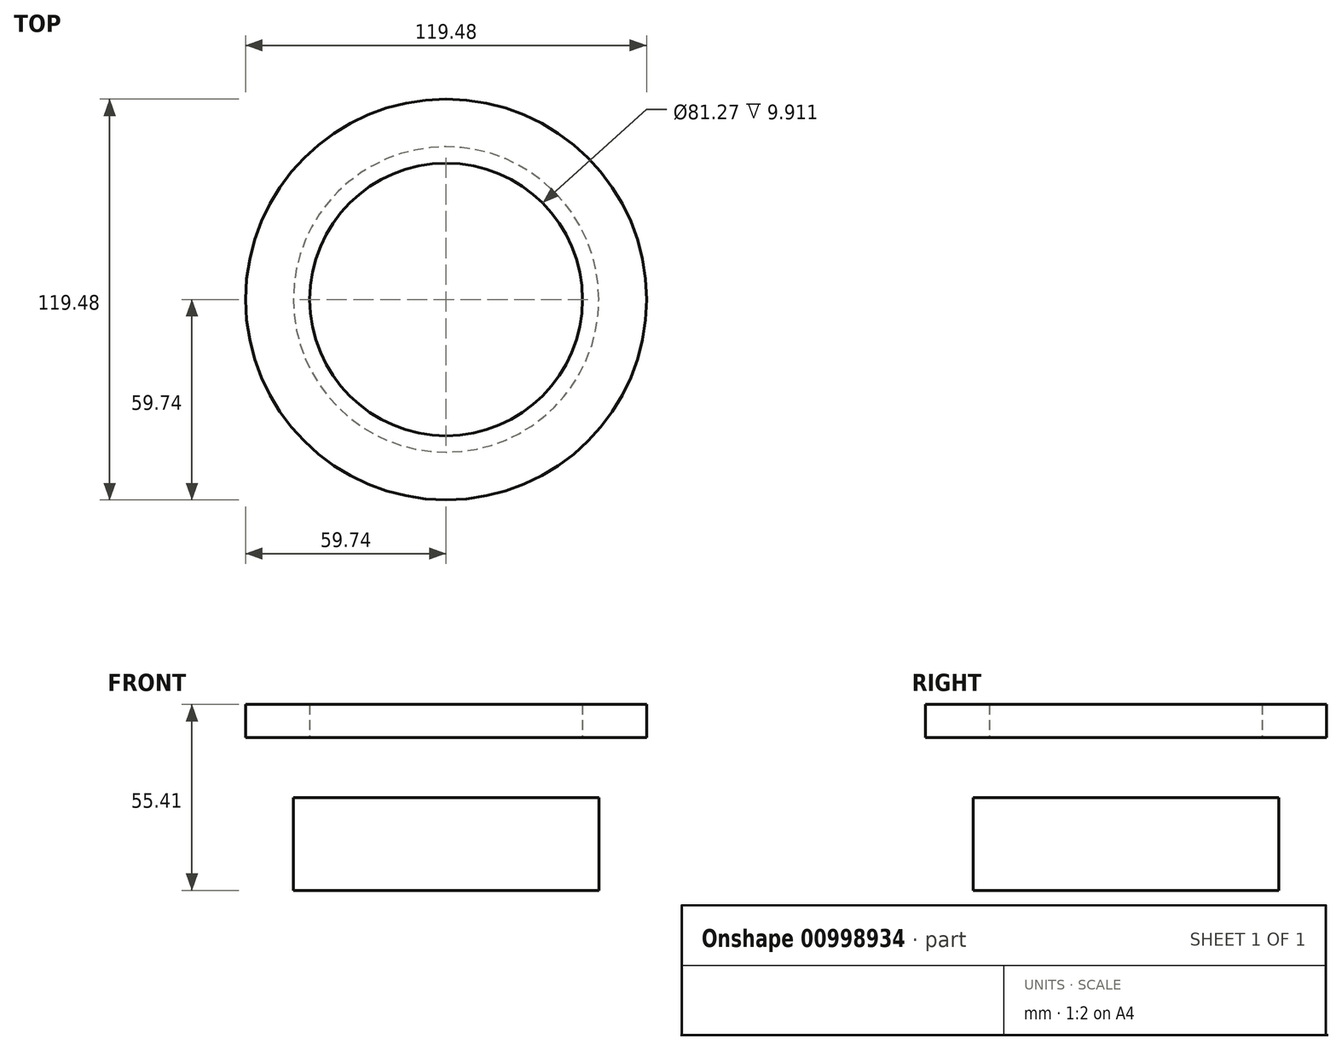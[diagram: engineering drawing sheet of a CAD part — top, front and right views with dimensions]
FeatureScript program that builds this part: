
annotation { "Feature Type Name" : "Feature", "Feature Type Description" : "" }
export const myFeature = defineFeature(function(context is Context, id is Id, definition is map)
    precondition{}
    {
        {
            var Q0;
            Q0=qCreatedBy(makeId("Front.planeOp"),FACE);
            var sketch = newSketch(context, id + "F0", { "sketchPlane" : qUnion([Q0])});
            skLineSegment(sketch, "E0.bottom", {"start": v(0, 0) * mm, "end": v(45.5, 0) * mm});
            skLineSegment(sketch, "E0.top", {"start": v(0, 27.66) * mm, "end": v(45.5, 27.66) * mm});
            skLineSegment(sketch, "E0.left", {"start": v(0, 0) * mm, "end": v(0, 27.66) * mm});
            skLineSegment(sketch, "E0.right", {"start": v(45.5, 0) * mm, "end": v(45.5, 27.66) * mm});
            skLineSegment(sketch, "E1.bottom", {"start": v(59.74, 55.41) * mm, "end": v(40.64, 55.41) * mm});
            skLineSegment(sketch, "E1.top", {"start": v(59.74, 45.5) * mm, "end": v(40.64, 45.5) * mm});
            skLineSegment(sketch, "E1.left", {"start": v(59.74, 55.41) * mm, "end": v(59.74, 45.5) * mm});
            skLineSegment(sketch, "E1.right", {"start": v(40.64, 55.41) * mm, "end": v(40.64, 45.5) * mm});
            skLineSegment(sketch, "E2", {"start": v(0, 0) * mm, "end": v(0, 79.92) * mm, "construction": true});
            skSolve(sketch);
        }
        {
            var Q0;
            Q0=makeQuery(id+"F0.imprint","IMPRINT",FACE,{"disambiguationData":[TD([[makeQuery(id+"F0.imprint","IMPRINT",EDGE,{"derivedFrom":sQuery(id+"F0.wireOp",EDGE,"E0.bottom")}),1.0]])]});
            var Q1;
            Q1=makeQuery(id+"F0.imprint","IMPRINT",FACE,{"disambiguationData":[TD([[makeQuery(id+"F0.imprint","IMPRINT",EDGE,{"derivedFrom":sQuery(id+"F0.wireOp",EDGE,"E1.bottom")}),1.0]])]});
            var Q2;
            Q2=sQuery(id+"F0.wireOp",EDGE,"E2");
            revolve(context, id + "F1", {"surfaceOperationType" : NewSurfaceOperationType.NEW, "entities" : qUnion([Q0, Q1]), "axis" : qUnion([Q2]), "revolveType" : RevolveType.FULL});
        }
    });
